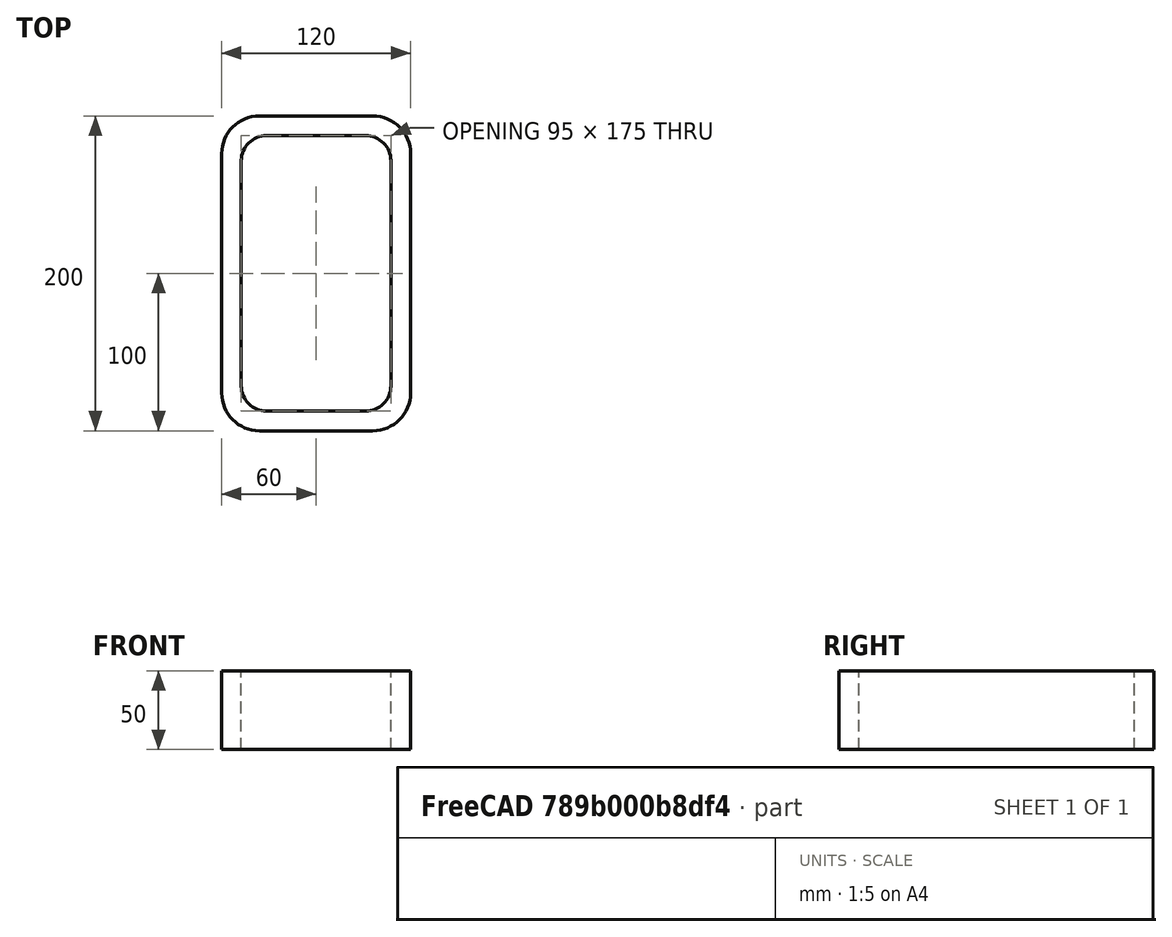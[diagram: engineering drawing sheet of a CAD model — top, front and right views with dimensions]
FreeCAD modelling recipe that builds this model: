
FCSTD DOCUMENT  (FreeCAD 0.15R4671 (Git))
Label: Rectangular hollow section 200x120x12.5 EN10219 S235JRH
License: All rights reserved
LicenseURL: http://en.wikipedia.org/wiki/All_rights_reserved
objects: Sketcher::SketchObject×1, Part::Extrusion×1
note: 2 computed .brp shape members not serialized (recipe doc carries the construction recipe); baked Part::Feature solids carry a one-line shape summary decoded from their .brp

FEATURE [Sketcher::SketchObject] Sketch
  sketch-geometry (16):
    g0: LineSegment StartX=-31.5 StartY=87.5 StartZ=0 EndX=31.5 EndY=87.5 EndZ=0
    g1: LineSegment StartX=47.5 StartY=71.5 StartZ=0 EndX=47.5 EndY=-71.5 EndZ=0
    g2: LineSegment StartX=31.5 StartY=-87.5 StartZ=0 EndX=-31.5 EndY=-87.5 EndZ=0
    g3: LineSegment StartX=-47.5 StartY=-71.5 StartZ=0 EndX=-47.5 EndY=71.5 EndZ=0
    g4: LineSegment StartX=-36 StartY=100 StartZ=0 EndX=36 EndY=100 EndZ=0
    g5: LineSegment StartX=60 StartY=76 StartZ=0 EndX=60 EndY=-76 EndZ=0
    g6: LineSegment StartX=36 StartY=-100 StartZ=0 EndX=-36 EndY=-100 EndZ=0
    g7: LineSegment StartX=-60 StartY=-76 StartZ=0 EndX=-60 EndY=76 EndZ=0
    g8: ArcOfCircle CenterX=-31.5 CenterY=71.5 CenterZ=0 NormalX=0 NormalY=0 NormalZ=1 Radius=16 StartAngle=1.5708 EndAngle=3.14159
    g9: ArcOfCircle CenterX=31.5 CenterY=71.5 CenterZ=0 NormalX=0 NormalY=0 NormalZ=1 Radius=16 StartAngle=0 EndAngle=1.5708
    g10: ArcOfCircle CenterX=31.5 CenterY=-71.5 CenterZ=0 NormalX=0 NormalY=0 NormalZ=1 Radius=16 StartAngle=4.71239 EndAngle=6.28319
    g11: ArcOfCircle CenterX=-31.5 CenterY=-71.5 CenterZ=0 NormalX=0 NormalY=0 NormalZ=1 Radius=16 StartAngle=3.14159 EndAngle=4.71239
    g12: ArcOfCircle CenterX=36 CenterY=76 CenterZ=0 NormalX=0 NormalY=0 NormalZ=1 Radius=24 StartAngle=0 EndAngle=1.5708
    g13: ArcOfCircle CenterX=36 CenterY=-76 CenterZ=0 NormalX=0 NormalY=0 NormalZ=1 Radius=24 StartAngle=4.71239 EndAngle=6.28319
    g14: ArcOfCircle CenterX=-36 CenterY=-76 CenterZ=0 NormalX=0 NormalY=0 NormalZ=1 Radius=24 StartAngle=3.14159 EndAngle=4.71239
    g15: ArcOfCircle CenterX=-36 CenterY=76 CenterZ=0 NormalX=0 NormalY=0 NormalZ=1 Radius=24 StartAngle=1.5708 EndAngle=3.14159
  constraints (36):
    c: Horizontal(g2)
    c: Vertical(g3)
    c: Horizontal(g6)
    c: Vertical(g7)
    c: Tangent(g3,g8) = 1.5708
    c: Tangent(g0,g8) = 1.5708
    c: Tangent(g0,g9) = 1.5708
    c: Tangent(g1,g9) = 1.5708
    c: Tangent(g1,g10) = 1.5708
    c: Tangent(g2,g10) = 1.5708
    c: Tangent(g2,g11) = 1.5708
    c: Tangent(g3,g11) = 1.5708
    c: Tangent(g4,g12) = 1.5708
    c: Tangent(g5,g12) = 1.5708
    c: Tangent(g5,g13) = 1.5708
    c: Tangent(g6,g13) = 1.5708
    c: Tangent(g6,g14) = 1.5708
    c: Tangent(g7,g14) = 1.5708
    c: Tangent(g7,g15) = 1.5708
    c: Tangent(g4,g15) = 1.5708
    c: Equal(g9,g8)
    c: Equal(g9,g11)
    c: Equal(g9,g10)
    c: Equal(g12,g15)
    c: Equal(g12,g14)
    c: Equal(g12,g13)
    c: Symmetric(g4,g6,g-1)
    c: Symmetric(g7,g5,g-2)
    c: DistanceY(g4,g6) = -200
    c: DistanceX(g7,g5) = 120
    c: Symmetric(g3,g1,g-2)
    c: Symmetric(g0,g2,g-1)
    c: DistanceY(g0,g4) = 12.5
    c: DistanceX(g5,g1) = -12.5
    c: Radius(g9) = 16
    c: Radius(g12) = 24
FEATURE [Part::Extrusion] Extrude  label="Rectangular hollow section 200x120x12.5 EN10219 S235JRH"
  Base = -> Sketch
  Dir = (0,0,50)
  Solid = true
